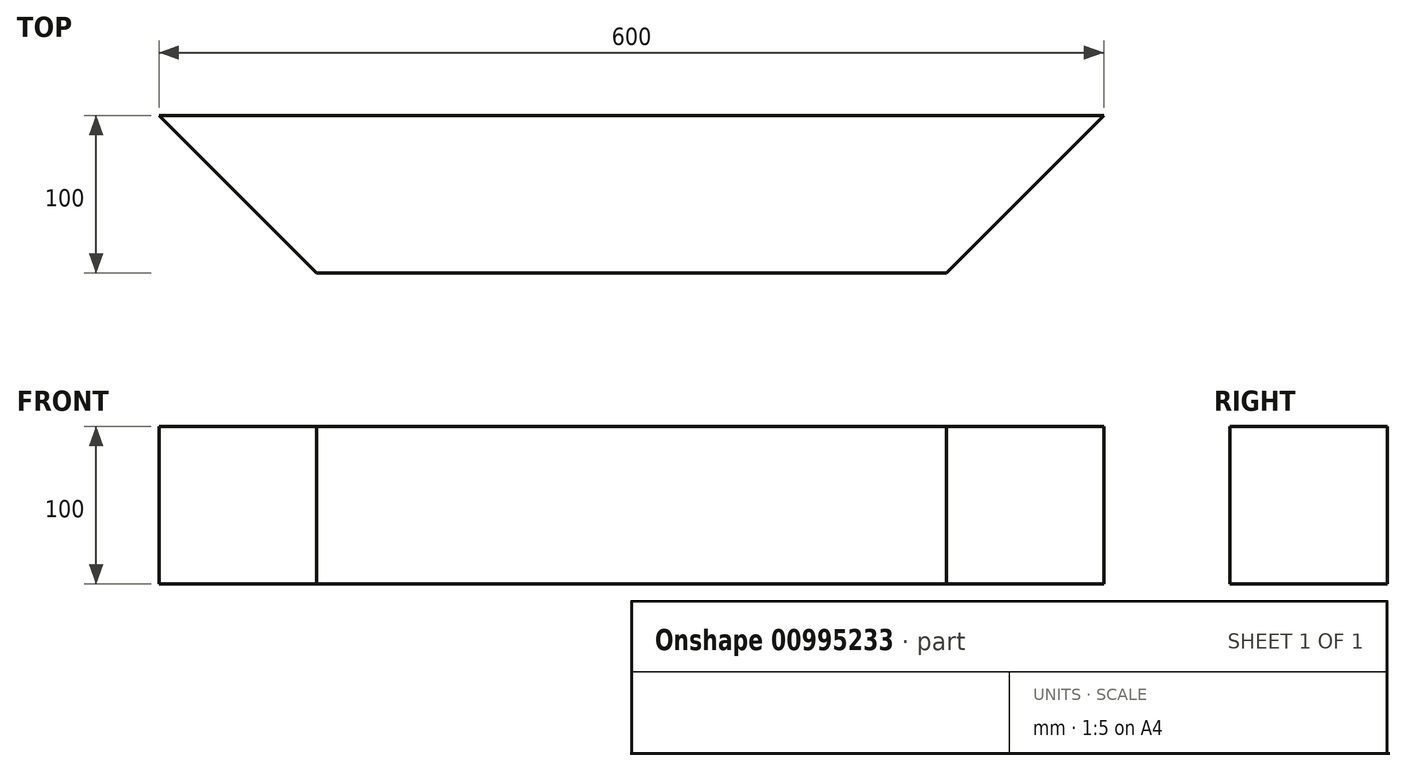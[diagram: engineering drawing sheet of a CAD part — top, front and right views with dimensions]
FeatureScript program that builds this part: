
annotation { "Feature Type Name" : "Feature", "Feature Type Description" : "" }
export const myFeature = defineFeature(function(context is Context, id is Id, definition is map)
    precondition{}
    {
        {
            var Q0;
            Q0=qCreatedBy(makeId("Front.planeOp"),FACE);
            var sketch = newSketch(context, id + "F0", { "sketchPlane" : qUnion([Q0])});
            skLineSegment(sketch, "E0.bottom", {"start": v(300, -50) * mm, "end": v(-300, -50) * mm});
            skLineSegment(sketch, "E0.top", {"start": v(300, 50) * mm, "end": v(-300, 50) * mm});
            skLineSegment(sketch, "E0.left", {"start": v(300, -50) * mm, "end": v(300, 50) * mm});
            skLineSegment(sketch, "E0.right", {"start": v(-300, -50) * mm, "end": v(-300, 50) * mm});
            skPoint(sketch, "E0.middle", {"position": v(0, 0) * mm});
            skSolve(sketch);
        }
        {
            var Q0;
            Q0 = qSketchRegion(id + "F0", true);
            extrude(context, id + "F1", {"entities" : qUnion([Q0]), "depth" : 100 * mm, "offsetDistance" : 25 * mm});
        }
        {
            var Q0;
            Q0=makeQuery(id+"F1.opExtrude","SWEPT_FACE",FACE,{"disambiguationData":[OSD([sQuery(id+"F0.wireOp",EDGE,"E0.top")])]});
            var sketch = newSketch(context, id + "F2", { "sketchPlane" : qUnion([Q0])});
            skLineSegment(sketch, "E1", {"start": v(-300, 0) * mm, "end": v(-200, -100) * mm});
            skLineSegment(sketch, "E2", {"start": v(300, 0) * mm, "end": v(200, -100) * mm});
            skSolve(sketch);
        }
        {
            var Q0;
            {var subQ0=sQuery(id+"F2.wireOp",EDGE,"E1");Q0=makeQuery(id+"F2.imprint","IMPRINT",FACE,{"disambiguationData":[TD([[makeQuery(id+"F2.imprint","IMPRINT",EDGE,{"derivedFrom":subQ0}),-1.0]])]});}
            extrude(context, id + "F3", {"entities" : qUnion([Q0]), "operationType" : NewBodyOperationType.REMOVE, "endBound" : BoundingType.THROUGH_ALL, "oppositeDirection" : true, "depth" : 25 * mm, "offsetDistance" : 25 * mm});
        }
        {
            var Q0;
            {var subQ0=sQuery(id+"F2.wireOp",EDGE,"E2");Q0=makeQuery(id+"F2.imprint","IMPRINT",FACE,{"disambiguationData":[TD([[makeQuery(id+"F2.imprint","IMPRINT",EDGE,{"derivedFrom":subQ0}),1.0]])]});}
            extrude(context, id + "F4", {"entities" : qUnion([Q0]), "operationType" : NewBodyOperationType.REMOVE, "endBound" : BoundingType.THROUGH_ALL, "oppositeDirection" : true, "depth" : 25 * mm, "offsetDistance" : 25 * mm});
        }
    });
